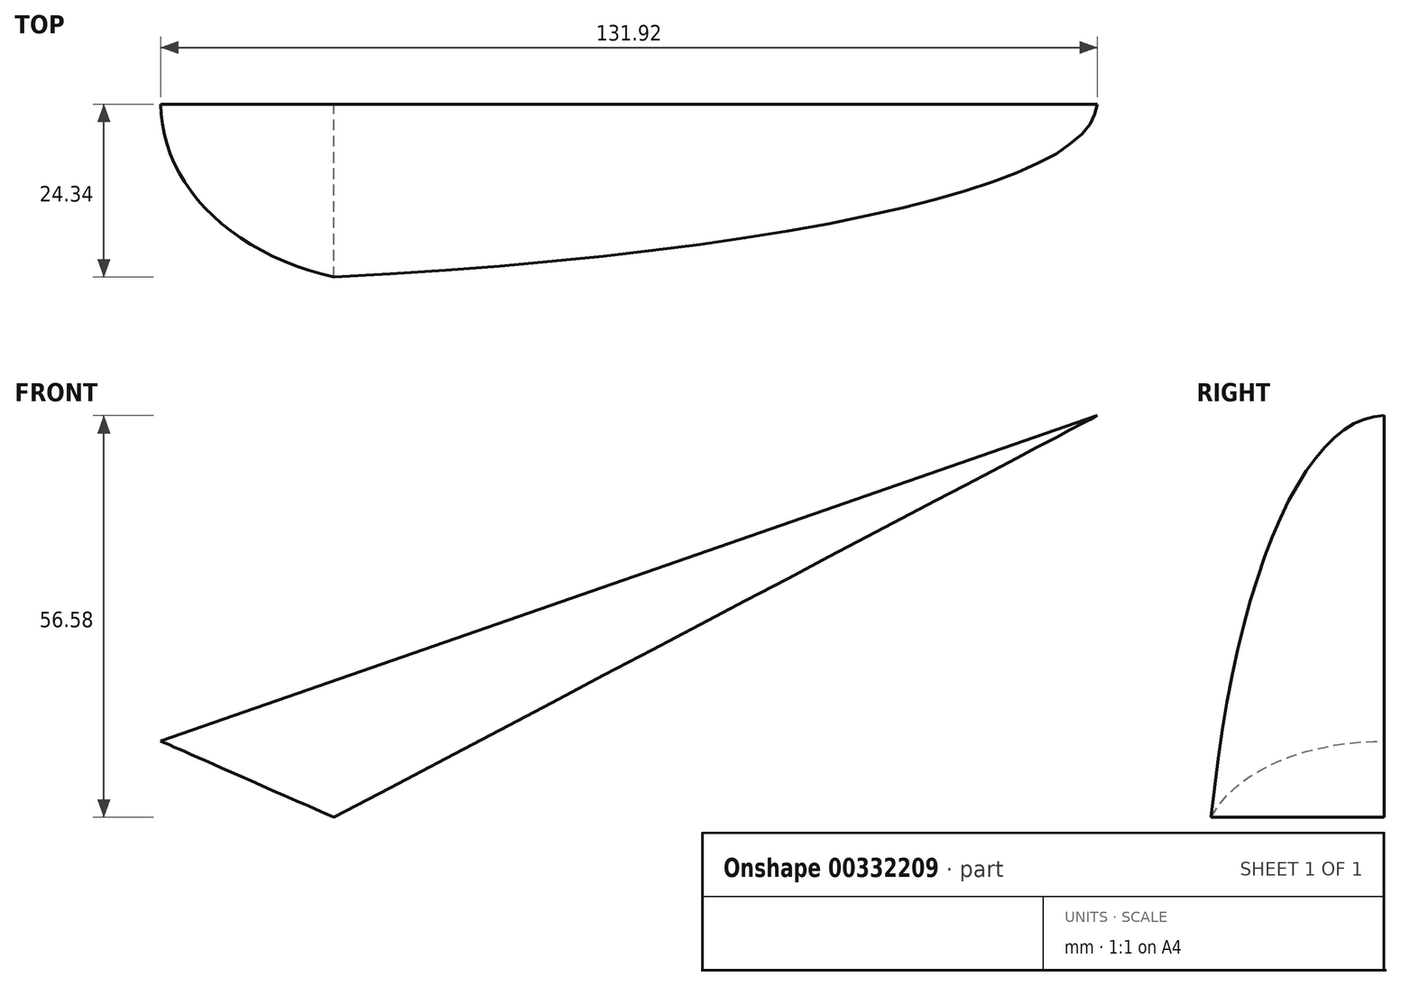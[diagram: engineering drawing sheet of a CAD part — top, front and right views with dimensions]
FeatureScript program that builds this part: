
annotation { "Feature Type Name" : "Feature", "Feature Type Description" : "" }
export const myFeature = defineFeature(function(context is Context, id is Id, definition is map)
    precondition{}
    {
        {
            var Q0;
            Q0=qCreatedBy(makeId("Front.planeOp"),FACE);
            var sketch = newSketch(context, id + "F0", { "sketchPlane" : qUnion([Q0])});
            skLineSegment(sketch, "E0", {"start": v(-7.3, 54.36) * mm, "end": v(-11.05, 51.68) * mm});
            skLineSegment(sketch, "E1", {"start": v(-116.69, -17.23) * mm, "end": v(15.23, 28.62) * mm});
            skLineSegment(sketch, "E2", {"start": v(15.23, 28.62) * mm, "end": v(-92.29, -27.96) * mm});
            skLineSegment(sketch, "E3", {"start": v(-92.29, -27.96) * mm, "end": v(-116.69, -17.23) * mm});
            skSolve(sketch);
        }
        {
            var Q0;
            Q0=makeQuery(id+"F0.imprint","IMPRINT",FACE,{"disambiguationData":[TD([[makeQuery(id+"F0.imprint","IMPRINT",EDGE,{"derivedFrom":sQuery(id+"F0.wireOp",EDGE,"E1")}),-1.0]])]});
            extrude(context, id + "F1", {"entities" : qUnion([Q0]), "endBound" : BoundingType.SYMMETRIC, "depth" : 25.4 * mm});
        }
        {
            var Q0;
            Q0=makeQuery(id+"F1.opExtrude","CAP_EDGE",EDGE,{"disambiguationData":[OSD([sQuery(id+"F0.wireOp",EDGE,"E1")])],"isStart":false});
            fillet(context, id + "F2", {"entities" : qUnion([Q0]), "radius" : 25.4 * mm, "tangentPropagation" : true, "allowEdgeOverflow" : false});
        }
    });
